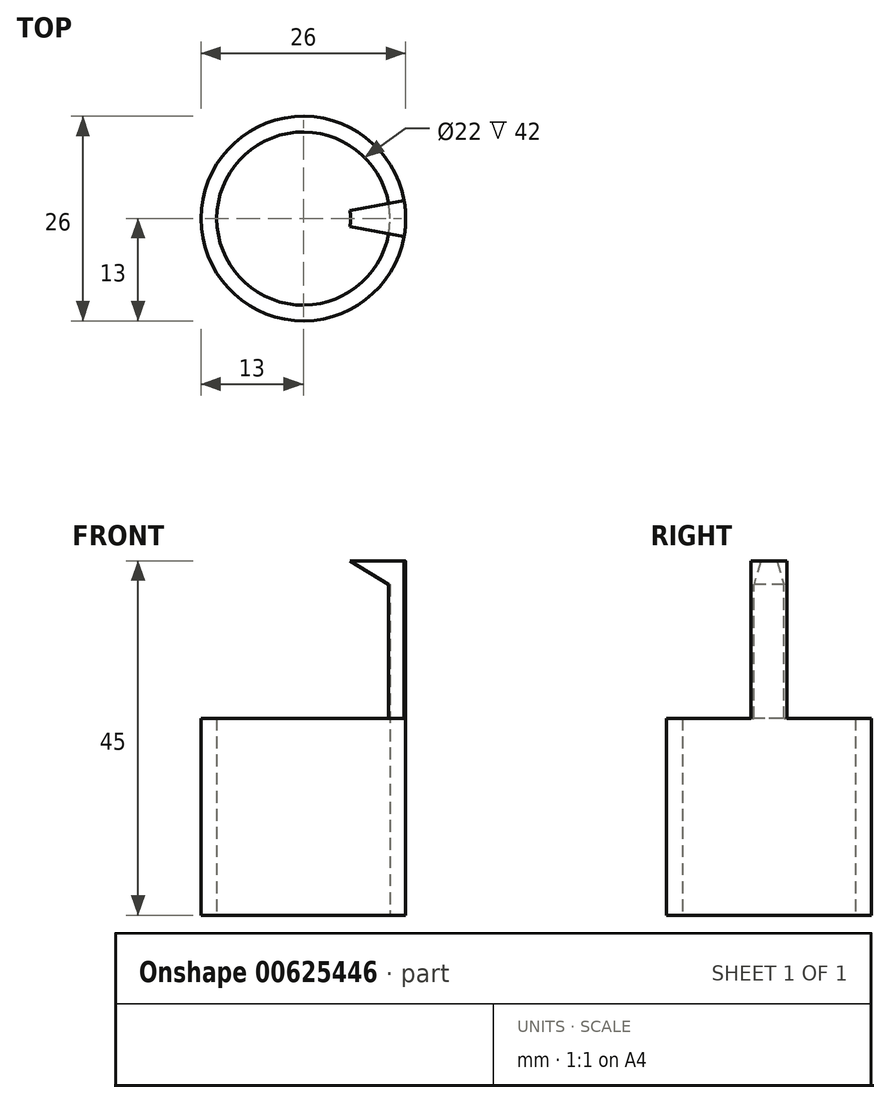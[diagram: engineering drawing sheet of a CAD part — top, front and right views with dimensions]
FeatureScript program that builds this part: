
annotation { "Feature Type Name" : "Feature", "Feature Type Description" : "" }
export const myFeature = defineFeature(function(context is Context, id is Id, definition is map)
    precondition{}
    {
        {
            var Q0;
            Q0=qCreatedBy(makeId("Top.planeOp"),FACE);
            var sketch = newSketch(context, id + "F0", { "sketchPlane" : qUnion([Q0])});
            skCircle(sketch, "E0", {"center": v(0, 0) * mm, "radius": 11 * mm});
            skCircle(sketch, "E1", {"center": v(0, 0) * mm, "radius": 13 * mm});
            skSolve(sketch);
        }
        {
            var Q0;
            Q0=makeQuery(id+"F0.imprint","IMPRINT",FACE,{"disambiguationData":[TD([[makeQuery(id+"F0.imprint","IMPRINT",EDGE,{"derivedFrom":sQuery(id+"F0.wireOp",EDGE,"E0")}),-1.0]])]});
            extrude(context, id + "F1", {"entities" : qUnion([Q0]), "depth" : 25 * mm, "offsetDistance" : 25 * mm});
        }
        {
            var Q0;
            Q0=qCreatedBy(makeId("Front.planeOp"),FACE);
            var sketch = newSketch(context, id + "F2", { "sketchPlane" : qUnion([Q0])});
            skLineSegment(sketch, "E2.bottom", {"start": v(13, 25) * mm, "end": v(11, 25) * mm});
            skLineSegment(sketch, "E2.top", {"start": v(13, 45) * mm, "end": v(11, 45) * mm});
            skLineSegment(sketch, "E2.left", {"start": v(13, 25) * mm, "end": v(13, 45) * mm});
            skLineSegment(sketch, "E2.right", {"start": v(11, 25) * mm, "end": v(11, 45) * mm});
            skLineSegment(sketch, "E3", {"start": v(11, 45) * mm, "end": v(6, 45) * mm});
            skLineSegment(sketch, "E4", {"start": v(6, 45) * mm, "end": v(11, 42) * mm});
            skLineSegment(sketch, "E5", {"start": v(0, 0) * mm, "end": v(0, 67) * mm, "construction": true});
            skSolve(sketch);
        }
        {
            var Q0;
            {var subQ0=sQuery(id+"F2.wireOp",EDGE,"E3");Q0=makeQuery(id+"F2.imprint","IMPRINT",FACE,{"disambiguationData":[TD([[makeQuery(id+"F2.imprint","IMPRINT",EDGE,{"derivedFrom":subQ0}),1.0]])]});}
            var Q1;
            {var subQ1=sQuery(id+"F2.wireOp",EDGE,"E2.bottom");Q1=makeQuery(id+"F2.imprint","IMPRINT",FACE,{"disambiguationData":[TD([[makeQuery(id+"F2.imprint","IMPRINT",EDGE,{"derivedFrom":subQ1}),-1.0]])]});}
            var Q2;
            Q2=sQuery(id+"F2.wireOp",EDGE,"E5");
            revolve(context, id + "F3", {"operationType" : NewBodyOperationType.ADD, "entities" : qUnion([Q0, Q1]), "axis" : qUnion([Q2]), "revolveType" : RevolveType.SYMMETRIC, "angle" : 20 * degree});
        }
    });
